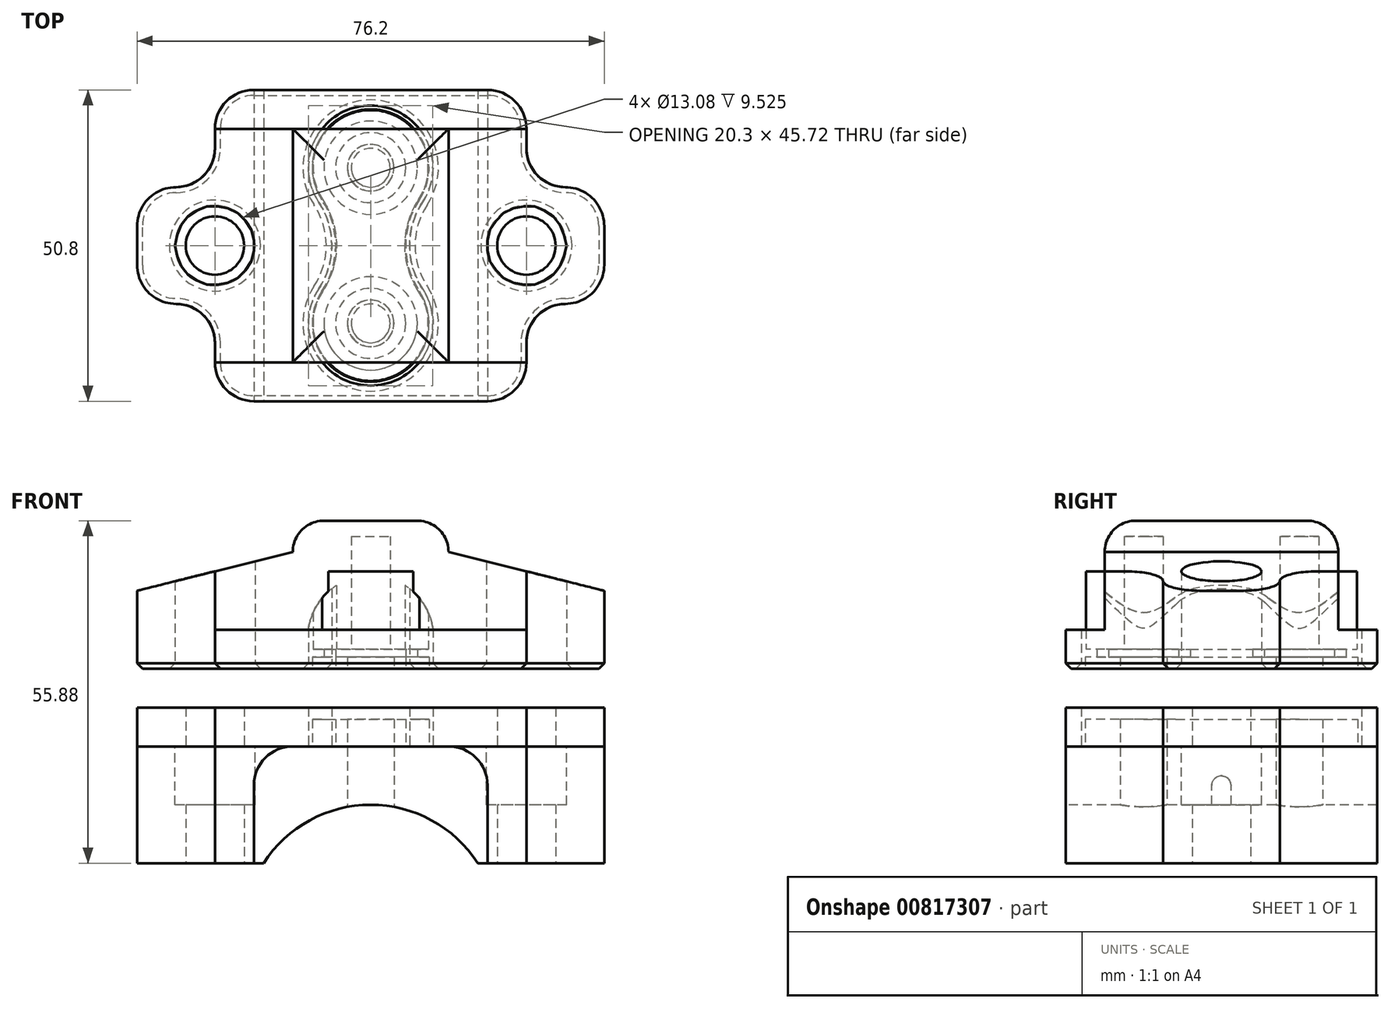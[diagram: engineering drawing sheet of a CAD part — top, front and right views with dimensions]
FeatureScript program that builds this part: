
annotation { "Feature Type Name" : "Feature", "Feature Type Description" : "" }
export const myFeature = defineFeature(function(context is Context, id is Id, definition is map)
    precondition{}
    {
        {
            var Q0;
            Q0=qCreatedBy(makeId("Top.planeOp"),FACE);
            var sketch = newSketch(context, id + "F0", { "sketchPlane" : qUnion([Q0])});
            skLineSegment(sketch, "E0.bottom", {"start": v(31.75, -9.52) * mm, "end": v(31.75, -9.52) * mm});
            skLineSegment(sketch, "E0.top", {"start": v(31.75, 9.53) * mm, "end": v(31.75, 9.53) * mm});
            skLineSegment(sketch, "E0.left", {"start": v(38.1, -3.17) * mm, "end": v(38.1, 3.17) * mm});
            skLineSegment(sketch, "E0.right", {"start": v(-38.1, -3.18) * mm, "end": v(-38.1, 3.17) * mm});
            skPoint(sketch, "E0.middle", {"position": v(0, 0) * mm});
            skLineSegment(sketch, "E1.bottom", {"start": v(19.05, -25.4) * mm, "end": v(-19.05, -25.4) * mm});
            skLineSegment(sketch, "E1.top", {"start": v(19.05, 25.4) * mm, "end": v(-19.05, 25.4) * mm});
            skLineSegment(sketch, "E1.left", {"start": v(25.4, -19.05) * mm, "end": v(25.4, -15.88) * mm});
            skLineSegment(sketch, "E1.right", {"start": v(-25.4, -19.05) * mm, "end": v(-25.4, -15.88) * mm});
            skLineSegment(sketch, "E2.trimOffspring", {"start": v(-25.4, 15.88) * mm, "end": v(-25.4, 19.05) * mm});
            skLineSegment(sketch, "E3.trimOffspring", {"start": v(-31.75, 9.52) * mm, "end": v(-31.75, 9.52) * mm});
            skLineSegment(sketch, "E4.trimOffspring", {"start": v(25.4, 15.88) * mm, "end": v(25.4, 19.05) * mm});
            skLineSegment(sketch, "E5.trimOffspring", {"start": v(-31.75, -9.53) * mm, "end": v(-31.75, -9.53) * mm});
            skCircle(sketch, "E6", {"center": v(-25.4, 0) * mm, "radius": 4.76 * mm});
            skCircle(sketch, "E7", {"center": v(25.4, 0) * mm, "radius": 4.76 * mm});
            skPoint(sketch, "E8", {"position": v(-31.75, 9.52) * mm});
            skPoint(sketch, "E9", {"position": v(31.75, 9.53) * mm});
            skPoint(sketch, "E10.visualSharp", {"position": v(-38.1, -9.53) * mm});
            skArc(sketch, "E10.filletArc", {"start": v(-38.1, -3.18) * mm, "mid": v(-36.24, -7.67) * mm, "end": v(-31.75, -9.53) * mm});
            skPoint(sketch, "E11.visualSharp", {"position": v(-38.1, 9.52) * mm});
            skArc(sketch, "E11.filletArc", {"start": v(-31.75, 9.53) * mm, "mid": v(-36.24, 7.67) * mm, "end": v(-38.1, 3.17) * mm});
            skPoint(sketch, "E12.visualSharp", {"position": v(-25.4, 9.52) * mm});
            skArc(sketch, "E12.filletArc", {"start": v(-31.75, 9.52) * mm, "mid": v(-27.26, 11.38) * mm, "end": v(-25.4, 15.88) * mm});
            skPoint(sketch, "E13.visualSharp", {"position": v(25.4, 9.53) * mm});
            skArc(sketch, "E13.filletArc", {"start": v(25.4, 15.88) * mm, "mid": v(27.26, 11.38) * mm, "end": v(31.75, 9.52) * mm});
            skPoint(sketch, "E14.visualSharp", {"position": v(38.1, 9.53) * mm});
            skArc(sketch, "E14.filletArc", {"start": v(38.1, 3.17) * mm, "mid": v(36.24, 7.67) * mm, "end": v(31.75, 9.53) * mm});
            skPoint(sketch, "E15.visualSharp", {"position": v(38.1, -9.52) * mm});
            skArc(sketch, "E15.filletArc", {"start": v(31.75, -9.53) * mm, "mid": v(36.24, -7.67) * mm, "end": v(38.1, -3.17) * mm});
            skPoint(sketch, "E16.visualSharp", {"position": v(25.4, -9.52) * mm});
            skArc(sketch, "E16.filletArc", {"start": v(31.75, -9.52) * mm, "mid": v(27.26, -11.38) * mm, "end": v(25.4, -15.88) * mm});
            skPoint(sketch, "E17.visualSharp", {"position": v(-25.4, -9.53) * mm});
            skArc(sketch, "E17.filletArc", {"start": v(-25.4, -15.88) * mm, "mid": v(-27.26, -11.38) * mm, "end": v(-31.75, -9.53) * mm});
            skPoint(sketch, "E18.visualSharp", {"position": v(25.4, 25.4) * mm});
            skArc(sketch, "E18.filletArc", {"start": v(25.4, 19.05) * mm, "mid": v(23.54, 23.54) * mm, "end": v(19.05, 25.4) * mm});
            skPoint(sketch, "E19.visualSharp", {"position": v(25.4, -25.4) * mm});
            skArc(sketch, "E19.filletArc", {"start": v(19.05, -25.4) * mm, "mid": v(23.54, -23.54) * mm, "end": v(25.4, -19.05) * mm});
            skPoint(sketch, "E20.visualSharp", {"position": v(-25.4, -25.4) * mm});
            skArc(sketch, "E20.filletArc", {"start": v(-25.4, -19.05) * mm, "mid": v(-23.54, -23.54) * mm, "end": v(-19.05, -25.4) * mm});
            skPoint(sketch, "E21.visualSharp", {"position": v(-25.4, 25.4) * mm});
            skArc(sketch, "E21.filletArc", {"start": v(-19.05, 25.4) * mm, "mid": v(-23.54, 23.54) * mm, "end": v(-25.4, 19.05) * mm});
            skCircle(sketch, "E22", {"center": v(0, 12.7) * mm, "radius": 3.18 * mm, "construction": true});
            skCircle(sketch, "E23", {"center": v(0, -12.7) * mm, "radius": 3.18 * mm, "construction": true});
            skArc(sketch, "E24", {"start": v(8.48, 7.1) * mm, "mid": v(0, 22.86) * mm, "end": v(-8.48, 7.1) * mm});
            skArc(sketch, "E25", {"start": v(-8.48, -7.1) * mm, "mid": v(0, -22.86) * mm, "end": v(8.48, -7.1) * mm});
            skArc(sketch, "E26", {"start": v(8.48, 7.1) * mm, "mid": v(6.35, 0) * mm, "end": v(8.48, -7.1) * mm});
            skArc(sketch, "E27", {"start": v(-8.48, -7.1) * mm, "mid": v(-6.35, 0) * mm, "end": v(-8.48, 7.1) * mm});
            skSolve(sketch);
        }
        {
            var Q0;
            Q0 = qSketchRegion(id + "F0", true);
            extrude(context, id + "F1", {"entities" : qUnion([Q0]), "depth" : 25.4 * mm, "offsetDistance" : 25.4 * mm});
        }
        {
            var Q0;
            Q0=qCreatedBy(makeId("Front.planeOp"),FACE);
            var sketch = newSketch(context, id + "F2", { "sketchPlane" : qUnion([Q0])});
            skLineSegment(sketch, "E28.bottom", {"start": v(19.05, -19.05) * mm, "end": v(-19.05, -19.05) * mm});
            skLineSegment(sketch, "E28.top", {"start": v(12.7, 19.05) * mm, "end": v(-12.7, 19.05) * mm});
            skLineSegment(sketch, "E28.left", {"start": v(19.05, -19.05) * mm, "end": v(19.05, 12.7) * mm});
            skLineSegment(sketch, "E28.right", {"start": v(-19.05, -19.05) * mm, "end": v(-19.05, 12.7) * mm});
            skPoint(sketch, "E28.middle", {"position": v(0, 0) * mm});
            skPoint(sketch, "E29.visualSharp", {"position": v(-19.05, 19.05) * mm});
            skArc(sketch, "E29.filletArc", {"start": v(-12.7, 19.05) * mm, "mid": v(-17.2, 17.2) * mm, "end": v(-19.05, 12.7) * mm});
            skPoint(sketch, "E30.visualSharp", {"position": v(19.05, 19.05) * mm});
            skArc(sketch, "E30.filletArc", {"start": v(19.05, 12.7) * mm, "mid": v(17.2, 17.2) * mm, "end": v(12.7, 19.05) * mm});
            skSolve(sketch);
        }
        {
            var Q0;
            Q0 = qSketchRegion(id + "F2", true);
            extrude(context, id + "F3", {"entities" : qUnion([Q0]), "operationType" : NewBodyOperationType.REMOVE, "endBound" : BoundingType.SYMMETRIC, "oppositeDirection" : true, "depth" : 127 * mm, "offsetDistance" : 25.4 * mm});
        }
        {
            var Q0;
            Q0=makeQuery(id+"F1.opExtrude","CAP_FACE",FACE,{"disambiguationData":[OSD([sQuery(id+"F0.wireOp",EDGE,"E0.left"),sQuery(id+"F0.wireOp",EDGE,"E0.right"),sQuery(id+"F0.wireOp",EDGE,"E1.bottom"),sQuery(id+"F0.wireOp",EDGE,"E1.top"),sQuery(id+"F0.wireOp",EDGE,"E1.left"),sQuery(id+"F0.wireOp",EDGE,"E1.right"),sQuery(id+"F0.wireOp",EDGE,"E2.trimOffspring"),sQuery(id+"F0.wireOp",EDGE,"E4.trimOffspring"),sQuery(id+"F0.wireOp",EDGE,"E6"),sQuery(id+"F0.wireOp",EDGE,"E7"),sQuery(id+"F0.wireOp",EDGE,"E10.filletArc"),sQuery(id+"F0.wireOp",EDGE,"E11.filletArc"),sQuery(id+"F0.wireOp",EDGE,"E12.filletArc"),sQuery(id+"F0.wireOp",EDGE,"E13.filletArc"),sQuery(id+"F0.wireOp",EDGE,"E14.filletArc"),sQuery(id+"F0.wireOp",EDGE,"E15.filletArc"),sQuery(id+"F0.wireOp",EDGE,"E16.filletArc"),sQuery(id+"F0.wireOp",EDGE,"E17.filletArc"),sQuery(id+"F0.wireOp",EDGE,"E18.filletArc"),sQuery(id+"F0.wireOp",EDGE,"E19.filletArc"),sQuery(id+"F0.wireOp",EDGE,"E20.filletArc"),sQuery(id+"F0.wireOp",EDGE,"E21.filletArc"),sQuery(id+"F0.wireOp",EDGE,"E24"),sQuery(id+"F0.wireOp",EDGE,"E25"),sQuery(id+"F0.wireOp",EDGE,"E26"),sQuery(id+"F0.wireOp",EDGE,"E27")])],"isStart":false});
            cPlane(context, id + "F4", {"entities" : qUnion([Q0]), "cplaneType" : CPlaneType.OFFSET, "offset" : 6.35 * mm, "width" : 152.4 * mm, "height" : 152.4 * mm});
        }
        {
            var Q0;
            Q0=qCreatedBy(id+"F4.planeOp",FACE);
            var sketch = newSketch(context, id + "F5", { "sketchPlane" : qUnion([Q0])});
            skArc(sketch, "E31.0.0", {"start": v(-25.4, 15.88) * mm, "mid": v(-27.26, 11.38) * mm, "end": v(-31.75, 9.52) * mm});
            skArc(sketch, "E31.0.1", {"start": v(-31.75, 9.53) * mm, "mid": v(-36.24, 7.67) * mm, "end": v(-38.1, 3.17) * mm});
            skLineSegment(sketch, "E31.0.2", {"start": v(-38.1, 3.17) * mm, "end": v(-38.1, -3.18) * mm});
            skArc(sketch, "E31.0.3", {"start": v(-38.1, -3.18) * mm, "mid": v(-36.24, -7.67) * mm, "end": v(-31.75, -9.53) * mm});
            skArc(sketch, "E31.0.4", {"start": v(-31.75, -9.53) * mm, "mid": v(-27.26, -11.38) * mm, "end": v(-25.4, -15.88) * mm});
            skLineSegment(sketch, "E31.0.5", {"start": v(-25.4, -15.88) * mm, "end": v(-25.4, -19.05) * mm});
            skArc(sketch, "E31.0.6", {"start": v(-25.4, -19.05) * mm, "mid": v(-23.54, -23.54) * mm, "end": v(-19.05, -25.4) * mm});
            skLineSegment(sketch, "E31.0.7", {"start": v(-19.05, -25.4) * mm, "end": v(19.05, -25.4) * mm});
            skArc(sketch, "E31.0.8", {"start": v(19.05, -25.4) * mm, "mid": v(23.54, -23.54) * mm, "end": v(25.4, -19.05) * mm});
            skLineSegment(sketch, "E31.0.9", {"start": v(25.4, -19.05) * mm, "end": v(25.4, -15.88) * mm});
            skArc(sketch, "E31.0.10", {"start": v(25.4, -15.88) * mm, "mid": v(27.26, -11.38) * mm, "end": v(31.75, -9.52) * mm});
            skArc(sketch, "E31.0.11", {"start": v(31.75, -9.53) * mm, "mid": v(36.24, -7.67) * mm, "end": v(38.1, -3.17) * mm});
            skLineSegment(sketch, "E31.0.12", {"start": v(38.1, -3.17) * mm, "end": v(38.1, 3.17) * mm});
            skArc(sketch, "E31.0.13", {"start": v(38.1, 3.17) * mm, "mid": v(36.24, 7.67) * mm, "end": v(31.75, 9.53) * mm});
            skArc(sketch, "E31.0.14", {"start": v(31.75, 9.52) * mm, "mid": v(27.26, 11.38) * mm, "end": v(25.4, 15.88) * mm});
            skLineSegment(sketch, "E31.0.15", {"start": v(25.4, 15.88) * mm, "end": v(25.4, 19.05) * mm});
            skArc(sketch, "E31.0.16", {"start": v(25.4, 19.05) * mm, "mid": v(23.54, 23.54) * mm, "end": v(19.05, 25.4) * mm});
            skLineSegment(sketch, "E31.0.17", {"start": v(19.05, 25.4) * mm, "end": v(-19.05, 25.4) * mm});
            skArc(sketch, "E31.0.18", {"start": v(-19.05, 25.4) * mm, "mid": v(-23.54, 23.54) * mm, "end": v(-25.4, 19.05) * mm});
            skLineSegment(sketch, "E31.0.19", {"start": v(-25.4, 19.05) * mm, "end": v(-25.4, 15.88) * mm});
            skCircle(sketch, "E32.0", {"center": v(25.4, 0) * mm, "radius": 4.76 * mm, "construction": true});
            skCircle(sketch, "E33.0", {"center": v(-25.4, 0) * mm, "radius": 4.76 * mm, "construction": true});
            skArc(sketch, "E34.0", {"start": v(8.48, 7.1) * mm, "mid": v(0, 22.86) * mm, "end": v(-8.48, 7.1) * mm});
            skArc(sketch, "E35.0", {"start": v(8.48, 7.1) * mm, "mid": v(6.35, 0) * mm, "end": v(8.48, -7.1) * mm});
            skArc(sketch, "E36.0", {"start": v(-8.48, -7.1) * mm, "mid": v(-6.35, 0) * mm, "end": v(-8.48, 7.1) * mm});
            skArc(sketch, "E37.0", {"start": v(-8.48, -7.1) * mm, "mid": v(0, -22.86) * mm, "end": v(8.48, -7.1) * mm});
            skCircle(sketch, "E38", {"center": v(25.4, 0) * mm, "radius": 6.54 * mm});
            skCircle(sketch, "E39", {"center": v(-25.4, 0) * mm, "radius": 6.54 * mm});
            skSolve(sketch);
        }
        {
            var Q0;
            Q0 = qSketchRegion(id + "F5", true);
            extrude(context, id + "F6", {"entities" : qUnion([Q0]), "depth" : 6.35 * mm, "offsetDistance" : 25.4 * mm});
        }
        {
            var Q0;
            Q0=qCreatedBy(id+"F4.planeOp",FACE);
            cPlane(context, id + "F7", {"entities" : qUnion([Q0]), "cplaneType" : CPlaneType.OFFSET, "offset" : 3.17 * mm, "width" : 152.4 * mm, "height" : 152.4 * mm});
        }
        {
            var Q0;
            Q0=qCreatedBy(id+"F7.planeOp",FACE);
            var sketch = newSketch(context, id + "F8", { "sketchPlane" : qUnion([Q0])});
            skArc(sketch, "E40.0", {"start": v(-8.48, -7.1) * mm, "mid": v(0, -22.86) * mm, "end": v(8.48, -7.1) * mm, "construction": true});
            skArc(sketch, "E41.0", {"start": v(8.48, 7.1) * mm, "mid": v(6.35, 0) * mm, "end": v(8.48, -7.1) * mm, "construction": true});
            skArc(sketch, "E42.0", {"start": v(-8.48, -7.1) * mm, "mid": v(-6.35, 0) * mm, "end": v(-8.48, 7.1) * mm, "construction": true});
            skArc(sketch, "E43.0", {"start": v(8.48, 7.1) * mm, "mid": v(0, 22.86) * mm, "end": v(-8.48, 7.1) * mm, "construction": true});
            skArc(sketch, "E44.0", {"start": v(-7.85, -7.53) * mm, "mid": v(0, -22.1) * mm, "end": v(7.85, -7.53) * mm});
            skArc(sketch, "E44.1", {"start": v(-7.85, -7.53) * mm, "mid": v(-5.59, 0) * mm, "end": v(-7.85, 7.53) * mm});
            skArc(sketch, "E44.2", {"start": v(7.85, 7.53) * mm, "mid": v(0, 22.1) * mm, "end": v(-7.85, 7.53) * mm});
            skArc(sketch, "E44.3", {"start": v(7.85, 7.53) * mm, "mid": v(5.59, 0) * mm, "end": v(7.85, -7.53) * mm});
            skSolve(sketch);
        }
        {
            var Q0;
            Q0 = qSketchRegion(id + "F8", true);
            extrude(context, id + "F9", {"entities" : qUnion([Q0]), "depth" : 12.7 * mm, "offsetDistance" : 25.4 * mm});
        }
        {
            var Q0;
            Q0=qCreatedBy(makeId("Top.planeOp"),FACE);
            var sketch = newSketch(context, id + "F10", { "sketchPlane" : qUnion([Q0])});
            skArc(sketch, "E45.0.0", {"start": v(-19.05, 25.4) * mm, "mid": v(-23.54, 23.54) * mm, "end": v(-25.4, 19.05) * mm});
            skLineSegment(sketch, "E45.0.1", {"start": v(-25.4, 19.05) * mm, "end": v(-25.4, 15.88) * mm});
            skArc(sketch, "E45.0.2", {"start": v(-25.4, 15.88) * mm, "mid": v(-27.26, 11.38) * mm, "end": v(-31.75, 9.52) * mm});
            skArc(sketch, "E45.0.3", {"start": v(-31.75, 9.53) * mm, "mid": v(-36.24, 7.67) * mm, "end": v(-38.1, 3.17) * mm});
            skLineSegment(sketch, "E45.0.4", {"start": v(-38.1, 3.17) * mm, "end": v(-38.1, -3.18) * mm});
            skArc(sketch, "E45.0.5", {"start": v(-38.1, -3.18) * mm, "mid": v(-36.24, -7.67) * mm, "end": v(-31.75, -9.53) * mm});
            skArc(sketch, "E45.0.6", {"start": v(-31.75, -9.52) * mm, "mid": v(-27.26, -11.38) * mm, "end": v(-25.4, -15.88) * mm});
            skLineSegment(sketch, "E45.0.7", {"start": v(-25.4, -15.88) * mm, "end": v(-25.4, -19.05) * mm});
            skArc(sketch, "E45.0.8", {"start": v(-25.4, -19.05) * mm, "mid": v(-23.54, -23.54) * mm, "end": v(-19.05, -25.4) * mm});
            skLineSegment(sketch, "E45.0.9", {"start": v(-19.05, -25.4) * mm, "end": v(19.05, -25.4) * mm});
            skArc(sketch, "E45.0.10", {"start": v(19.05, -25.4) * mm, "mid": v(23.54, -23.54) * mm, "end": v(25.4, -19.05) * mm});
            skLineSegment(sketch, "E45.0.11", {"start": v(25.4, -19.05) * mm, "end": v(25.4, -15.88) * mm});
            skArc(sketch, "E45.0.12", {"start": v(25.4, -15.88) * mm, "mid": v(27.26, -11.38) * mm, "end": v(31.75, -9.52) * mm});
            skArc(sketch, "E45.0.13", {"start": v(31.75, -9.53) * mm, "mid": v(36.24, -7.67) * mm, "end": v(38.1, -3.17) * mm});
            skLineSegment(sketch, "E45.0.14", {"start": v(38.1, -3.17) * mm, "end": v(38.1, 3.17) * mm});
            skArc(sketch, "E45.0.15", {"start": v(38.1, 3.17) * mm, "mid": v(36.24, 7.67) * mm, "end": v(31.75, 9.53) * mm});
            skArc(sketch, "E45.0.16", {"start": v(31.75, 9.52) * mm, "mid": v(27.26, 11.38) * mm, "end": v(25.4, 15.88) * mm});
            skLineSegment(sketch, "E45.0.17", {"start": v(25.4, 15.88) * mm, "end": v(25.4, 19.05) * mm});
            skArc(sketch, "E45.0.18", {"start": v(25.4, 19.05) * mm, "mid": v(23.54, 23.54) * mm, "end": v(19.05, 25.4) * mm});
            skLineSegment(sketch, "E45.0.19", {"start": v(19.05, 25.4) * mm, "end": v(-19.05, 25.4) * mm});
            skCircle(sketch, "E46.0", {"center": v(25.4, 0) * mm, "radius": 4.76 * mm});
            skCircle(sketch, "E47.0", {"center": v(-25.4, 0) * mm, "radius": 4.76 * mm});
            skCircle(sketch, "E48", {"center": v(0, 12.7) * mm, "radius": 3.81 * mm});
            skCircle(sketch, "E49", {"center": v(0, -12.7) * mm, "radius": 3.81 * mm});
            skSolve(sketch);
        }
        {
            var Q0;
            Q0 = qSketchRegion(id + "F10", true);
            extrude(context, id + "F11", {"entities" : qUnion([Q0]), "depth" : 19.05 * mm, "offsetDistance" : 25.4 * mm});
        }
        {
            var Q0;
            Q0=makeQuery(id+"F11.opExtrude","CAP_FACE",FACE,{"disambiguationData":[OSD([sQuery(id+"F10.wireOp",EDGE,"E45.0.0"),sQuery(id+"F10.wireOp",EDGE,"E45.0.1"),sQuery(id+"F10.wireOp",EDGE,"E45.0.2"),sQuery(id+"F10.wireOp",EDGE,"E45.0.3"),sQuery(id+"F10.wireOp",EDGE,"E45.0.4"),sQuery(id+"F10.wireOp",EDGE,"E45.0.5"),sQuery(id+"F10.wireOp",EDGE,"E45.0.6"),sQuery(id+"F10.wireOp",EDGE,"E45.0.7"),sQuery(id+"F10.wireOp",EDGE,"E45.0.8"),sQuery(id+"F10.wireOp",EDGE,"E45.0.9"),sQuery(id+"F10.wireOp",EDGE,"E45.0.10"),sQuery(id+"F10.wireOp",EDGE,"E45.0.11"),sQuery(id+"F10.wireOp",EDGE,"E45.0.12"),sQuery(id+"F10.wireOp",EDGE,"E45.0.13"),sQuery(id+"F10.wireOp",EDGE,"E45.0.14"),sQuery(id+"F10.wireOp",EDGE,"E45.0.15"),sQuery(id+"F10.wireOp",EDGE,"E45.0.16"),sQuery(id+"F10.wireOp",EDGE,"E45.0.17"),sQuery(id+"F10.wireOp",EDGE,"E45.0.18"),sQuery(id+"F10.wireOp",EDGE,"E45.0.19"),sQuery(id+"F10.wireOp",EDGE,"E46.0"),sQuery(id+"F10.wireOp",EDGE,"E47.0")])],"isStart":false});
            var sketch = newSketch(context, id + "F12", { "sketchPlane" : qUnion([Q0])});
            skArc(sketch, "E50.0", {"start": v(-8.48, -7.1) * mm, "mid": v(0, -22.86) * mm, "end": v(8.48, -7.1) * mm, "construction": true});
            skArc(sketch, "E51.0", {"start": v(8.48, 7.1) * mm, "mid": v(6.35, 0) * mm, "end": v(8.48, -7.1) * mm, "construction": true});
            skArc(sketch, "E52.0", {"start": v(8.48, 7.1) * mm, "mid": v(0, 22.86) * mm, "end": v(-8.48, 7.1) * mm, "construction": true});
            skArc(sketch, "E53.0", {"start": v(-8.48, -7.1) * mm, "mid": v(-6.35, 0) * mm, "end": v(-8.48, 7.1) * mm, "construction": true});
            skCircle(sketch, "E54.0", {"center": v(0, -12.7) * mm, "radius": 3.81 * mm});
            skCircle(sketch, "E55.0", {"center": v(0, 12.7) * mm, "radius": 3.81 * mm});
            skArc(sketch, "E56.0", {"start": v(-7.95, -7.46) * mm, "mid": v(0, -22.23) * mm, "end": v(7.95, -7.46) * mm});
            skArc(sketch, "E56.1", {"start": v(-7.95, -7.46) * mm, "mid": v(-5.72, 0) * mm, "end": v(-7.95, 7.46) * mm});
            skArc(sketch, "E56.2", {"start": v(7.95, 7.46) * mm, "mid": v(0, 22.23) * mm, "end": v(-7.95, 7.46) * mm});
            skArc(sketch, "E56.3", {"start": v(7.95, 7.46) * mm, "mid": v(5.72, 0) * mm, "end": v(7.95, -7.46) * mm});
            skSolve(sketch);
        }
        {
            var Q0;
            Q0 = qSketchRegion(id + "F12", true);
            extrude(context, id + "F13", {"entities" : qUnion([Q0]), "operationType" : NewBodyOperationType.ADD, "depth" : 4.44 * mm, "offsetDistance" : 25.4 * mm});
        }
        {
            var Q0;
            Q0=qCreatedBy(makeId("Front.planeOp"),FACE);
            var sketch = newSketch(context, id + "F14", { "sketchPlane" : qUnion([Q0])});
            skArc(sketch, "E57", {"start": v(17.46, 0) * mm, "mid": v(0, 9.53) * mm, "end": v(-17.46, 0) * mm});
            skLineSegment(sketch, "E58", {"start": v(-17.46, 0) * mm, "end": v(17.46, 0) * mm});
            skSolve(sketch);
        }
        {
            var Q0;
            Q0 = qSketchRegion(id + "F14", true);
            extrude(context, id + "F15", {"entities" : qUnion([Q0]), "operationType" : NewBodyOperationType.REMOVE, "endBound" : BoundingType.SYMMETRIC, "oppositeDirection" : true, "depth" : 127 * mm, "offsetDistance" : 25.4 * mm});
        }
        {
            var Q0;
            Q0=makeQuery(id+"F6.opExtrude","CAP_FACE",FACE,{"disambiguationData":[OSD([sQuery(id+"F5.wireOp",EDGE,"E31.0.0"),sQuery(id+"F5.wireOp",EDGE,"E31.0.1"),sQuery(id+"F5.wireOp",EDGE,"E31.0.2"),sQuery(id+"F5.wireOp",EDGE,"E31.0.3"),sQuery(id+"F5.wireOp",EDGE,"E31.0.4"),sQuery(id+"F5.wireOp",EDGE,"E31.0.5"),sQuery(id+"F5.wireOp",EDGE,"E31.0.6"),sQuery(id+"F5.wireOp",EDGE,"E31.0.7"),sQuery(id+"F5.wireOp",EDGE,"E31.0.8"),sQuery(id+"F5.wireOp",EDGE,"E31.0.9"),sQuery(id+"F5.wireOp",EDGE,"E31.0.10"),sQuery(id+"F5.wireOp",EDGE,"E31.0.11"),sQuery(id+"F5.wireOp",EDGE,"E31.0.12"),sQuery(id+"F5.wireOp",EDGE,"E31.0.13"),sQuery(id+"F5.wireOp",EDGE,"E31.0.14"),sQuery(id+"F5.wireOp",EDGE,"E31.0.15"),sQuery(id+"F5.wireOp",EDGE,"E31.0.16"),sQuery(id+"F5.wireOp",EDGE,"E31.0.17"),sQuery(id+"F5.wireOp",EDGE,"E31.0.18"),sQuery(id+"F5.wireOp",EDGE,"E31.0.19"),sQuery(id+"F5.wireOp",EDGE,"E34.0"),sQuery(id+"F5.wireOp",EDGE,"E35.0"),sQuery(id+"F5.wireOp",EDGE,"E36.0"),sQuery(id+"F5.wireOp",EDGE,"E37.0"),sQuery(id+"F5.wireOp",EDGE,"E38"),sQuery(id+"F5.wireOp",EDGE,"E39")])],"isStart":true});
            var sketch = newSketch(context, id + "F16", { "sketchPlane" : qUnion([Q0])});
            skArc(sketch, "E59.0", {"start": v(7.95, -7.46) * mm, "mid": v(5.72, 0) * mm, "end": v(7.95, 7.46) * mm});
            skArc(sketch, "E60.0", {"start": v(7.95, -7.46) * mm, "mid": v(0, -22.23) * mm, "end": v(-7.95, -7.46) * mm});
            skArc(sketch, "E61.0", {"start": v(-7.95, 7.46) * mm, "mid": v(-5.72, 0) * mm, "end": v(-7.95, -7.46) * mm});
            skArc(sketch, "E62.0", {"start": v(-7.95, 7.46) * mm, "mid": v(0, 22.23) * mm, "end": v(7.95, 7.46) * mm});
            skCircle(sketch, "E63.0", {"center": v(0, 12.7) * mm, "radius": 3.81 * mm});
            skCircle(sketch, "E64.0", {"center": v(0, -12.7) * mm, "radius": 3.81 * mm});
            skSolve(sketch);
        }
        {
            var Q0;
            Q0 = qSketchRegion(id + "F16", true);
            extrude(context, id + "F17", {"entities" : qUnion([Q0]), "oppositeDirection" : true, "depth" : 1.9 * mm, "offsetDistance" : 25.4 * mm});
        }
        {
            var Q0;
            Q0=makeQuery(id+"F6.opExtrude","CAP_FACE",FACE,{"disambiguationData":[OSD([sQuery(id+"F5.wireOp",EDGE,"E31.0.0"),sQuery(id+"F5.wireOp",EDGE,"E31.0.1"),sQuery(id+"F5.wireOp",EDGE,"E31.0.2"),sQuery(id+"F5.wireOp",EDGE,"E31.0.3"),sQuery(id+"F5.wireOp",EDGE,"E31.0.4"),sQuery(id+"F5.wireOp",EDGE,"E31.0.5"),sQuery(id+"F5.wireOp",EDGE,"E31.0.6"),sQuery(id+"F5.wireOp",EDGE,"E31.0.7"),sQuery(id+"F5.wireOp",EDGE,"E31.0.8"),sQuery(id+"F5.wireOp",EDGE,"E31.0.9"),sQuery(id+"F5.wireOp",EDGE,"E31.0.10"),sQuery(id+"F5.wireOp",EDGE,"E31.0.11"),sQuery(id+"F5.wireOp",EDGE,"E31.0.12"),sQuery(id+"F5.wireOp",EDGE,"E31.0.13"),sQuery(id+"F5.wireOp",EDGE,"E31.0.14"),sQuery(id+"F5.wireOp",EDGE,"E31.0.15"),sQuery(id+"F5.wireOp",EDGE,"E31.0.16"),sQuery(id+"F5.wireOp",EDGE,"E31.0.17"),sQuery(id+"F5.wireOp",EDGE,"E31.0.18"),sQuery(id+"F5.wireOp",EDGE,"E31.0.19"),sQuery(id+"F5.wireOp",EDGE,"E34.0"),sQuery(id+"F5.wireOp",EDGE,"E35.0"),sQuery(id+"F5.wireOp",EDGE,"E36.0"),sQuery(id+"F5.wireOp",EDGE,"E37.0"),sQuery(id+"F5.wireOp",EDGE,"E38"),sQuery(id+"F5.wireOp",EDGE,"E39")])],"isStart":true});
            var sketch = newSketch(context, id + "F18", { "sketchPlane" : qUnion([Q0])});
            skCircle(sketch, "E65", {"center": v(0, 12.7) * mm, "radius": 3.18 * mm});
            skCircle(sketch, "E66", {"center": v(0, -12.7) * mm, "radius": 3.18 * mm});
            skSolve(sketch);
        }
        {
            var Q0;
            Q0 = qSketchRegion(id + "F18", true);
            extrude(context, id + "F19", {"entities" : qUnion([Q0]), "oppositeDirection" : true, "depth" : 15.24 * mm, "offsetDistance" : 25.4 * mm});
        }
        {
            var Q0;
            Q0=makeQuery(id+"F19.opExtrude","CAP_FACE",FACE,{"disambiguationData":[OSD([sQuery(id+"F18.wireOp",EDGE,"E65")])],"isStart":false});
            var sketch = newSketch(context, id + "F20", { "sketchPlane" : qUnion([Q0])});
            skCircle(sketch, "E67", {"center": v(0, -12.7) * mm, "radius": 4.76 * mm});
            skCircle(sketch, "E68", {"center": v(0, 12.7) * mm, "radius": 4.76 * mm});
            skSolve(sketch);
        }
        {
            var Q0;
            Q0 = qSketchRegion(id + "F20", true);
            extrude(context, id + "F21", {"entities" : qUnion([Q0]), "operationType" : NewBodyOperationType.ADD, "depth" : 3.8 * mm, "offsetDistance" : 25.4 * mm});
        }
        {
            var Q0;
            Q0=makeQuery(id+"F11.opExtrude","CAP_FACE",FACE,{"disambiguationData":[OSD([sQuery(id+"F10.wireOp",EDGE,"E45.0.0"),sQuery(id+"F10.wireOp",EDGE,"E45.0.1"),sQuery(id+"F10.wireOp",EDGE,"E45.0.2"),sQuery(id+"F10.wireOp",EDGE,"E45.0.3"),sQuery(id+"F10.wireOp",EDGE,"E45.0.4"),sQuery(id+"F10.wireOp",EDGE,"E45.0.5"),sQuery(id+"F10.wireOp",EDGE,"E45.0.6"),sQuery(id+"F10.wireOp",EDGE,"E45.0.7"),sQuery(id+"F10.wireOp",EDGE,"E45.0.8"),sQuery(id+"F10.wireOp",EDGE,"E45.0.9"),sQuery(id+"F10.wireOp",EDGE,"E45.0.10"),sQuery(id+"F10.wireOp",EDGE,"E45.0.11"),sQuery(id+"F10.wireOp",EDGE,"E45.0.12"),sQuery(id+"F10.wireOp",EDGE,"E45.0.13"),sQuery(id+"F10.wireOp",EDGE,"E45.0.14"),sQuery(id+"F10.wireOp",EDGE,"E45.0.15"),sQuery(id+"F10.wireOp",EDGE,"E45.0.16"),sQuery(id+"F10.wireOp",EDGE,"E45.0.17"),sQuery(id+"F10.wireOp",EDGE,"E45.0.18"),sQuery(id+"F10.wireOp",EDGE,"E45.0.19"),sQuery(id+"F10.wireOp",EDGE,"E46.0"),sQuery(id+"F10.wireOp",EDGE,"E47.0"),sQuery(id+"F10.wireOp",EDGE,"E48"),sQuery(id+"F10.wireOp",EDGE,"E49")])],"isStart":false});
            var sketch = newSketch(context, id + "F22", { "sketchPlane" : qUnion([Q0])});
            skCircle(sketch, "E69.0", {"center": v(25.4, 0) * mm, "radius": 6.54 * mm});
            skCircle(sketch, "E70.0", {"center": v(-25.4, 0) * mm, "radius": 6.54 * mm});
            skSolve(sketch);
        }
        {
            var Q0;
            Q0 = qSketchRegion(id + "F22", true);
            extrude(context, id + "F23", {"entities" : qUnion([Q0]), "operationType" : NewBodyOperationType.REMOVE, "oppositeDirection" : true, "depth" : 9.52 * mm, "offsetDistance" : 25.4 * mm});
        }
        {
            var Q0;
            Q0=makeQuery(id+"F6.opExtrude","CAP_FACE",FACE,{"disambiguationData":[OSD([sQuery(id+"F5.wireOp",EDGE,"E31.0.0"),sQuery(id+"F5.wireOp",EDGE,"E31.0.1"),sQuery(id+"F5.wireOp",EDGE,"E31.0.2"),sQuery(id+"F5.wireOp",EDGE,"E31.0.3"),sQuery(id+"F5.wireOp",EDGE,"E31.0.4"),sQuery(id+"F5.wireOp",EDGE,"E31.0.5"),sQuery(id+"F5.wireOp",EDGE,"E31.0.6"),sQuery(id+"F5.wireOp",EDGE,"E31.0.7"),sQuery(id+"F5.wireOp",EDGE,"E31.0.8"),sQuery(id+"F5.wireOp",EDGE,"E31.0.9"),sQuery(id+"F5.wireOp",EDGE,"E31.0.10"),sQuery(id+"F5.wireOp",EDGE,"E31.0.11"),sQuery(id+"F5.wireOp",EDGE,"E31.0.12"),sQuery(id+"F5.wireOp",EDGE,"E31.0.13"),sQuery(id+"F5.wireOp",EDGE,"E31.0.14"),sQuery(id+"F5.wireOp",EDGE,"E31.0.15"),sQuery(id+"F5.wireOp",EDGE,"E31.0.16"),sQuery(id+"F5.wireOp",EDGE,"E31.0.17"),sQuery(id+"F5.wireOp",EDGE,"E31.0.18"),sQuery(id+"F5.wireOp",EDGE,"E31.0.19"),sQuery(id+"F5.wireOp",EDGE,"E34.0"),sQuery(id+"F5.wireOp",EDGE,"E35.0"),sQuery(id+"F5.wireOp",EDGE,"E36.0"),sQuery(id+"F5.wireOp",EDGE,"E37.0"),sQuery(id+"F5.wireOp",EDGE,"E38"),sQuery(id+"F5.wireOp",EDGE,"E39")])],"isStart":false});
            var sketch = newSketch(context, id + "F24", { "sketchPlane" : qUnion([Q0])});
            skCircle(sketch, "E71.0", {"center": v(-25.4, 0) * mm, "radius": 6.54 * mm});
            skCircle(sketch, "E72.0", {"center": v(25.4, 0) * mm, "radius": 6.54 * mm});
            skArc(sketch, "E73.0", {"start": v(-31.75, 9.53) * mm, "mid": v(-36.24, 7.67) * mm, "end": v(-38.1, 3.17) * mm});
            skArc(sketch, "E74.0", {"start": v(-38.1, -3.18) * mm, "mid": v(-36.24, -7.67) * mm, "end": v(-31.75, -9.53) * mm});
            skArc(sketch, "E75.0", {"start": v(-31.75, -9.52) * mm, "mid": v(-27.26, -11.38) * mm, "end": v(-25.4, -15.88) * mm});
            skArc(sketch, "E76.0", {"start": v(-25.4, 15.88) * mm, "mid": v(-27.26, 11.38) * mm, "end": v(-31.75, 9.52) * mm});
            skArc(sketch, "E77.0", {"start": v(25.4, -15.88) * mm, "mid": v(27.26, -11.38) * mm, "end": v(31.75, -9.52) * mm});
            skArc(sketch, "E78.0", {"start": v(31.75, -9.53) * mm, "mid": v(36.24, -7.67) * mm, "end": v(38.1, -3.17) * mm});
            skPoint(sketch, "E79.0", {"position": v(38.1, 3.17) * mm});
            skPoint(sketch, "E80.0", {"position": v(31.75, 9.53) * mm});
            skArc(sketch, "E81.0", {"start": v(31.75, 9.52) * mm, "mid": v(27.26, 11.38) * mm, "end": v(25.4, 15.88) * mm});
            skArc(sketch, "E82.0", {"start": v(38.1, 3.17) * mm, "mid": v(36.24, 7.67) * mm, "end": v(31.75, 9.53) * mm});
            skLineSegment(sketch, "E83.0", {"start": v(38.1, -3.17) * mm, "end": v(38.1, 3.17) * mm});
            skLineSegment(sketch, "E84.0", {"start": v(-25.4, -15.88) * mm, "end": v(-25.4, -19.05) * mm});
            skLineSegment(sketch, "E85.0.0", {"start": v(-25.4, 19.05) * mm, "end": v(-25.4, 15.88) * mm});
            skLineSegment(sketch, "E85.0.2", {"start": v(-25.4, 15.88) * mm, "end": v(-25.4, 19.05) * mm});
            skLineSegment(sketch, "E86.0", {"start": v(25.4, 15.88) * mm, "end": v(25.4, 19.05) * mm});
            skLineSegment(sketch, "E87.0", {"start": v(25.4, -19.05) * mm, "end": v(25.4, -15.88) * mm});
            skLineSegment(sketch, "E88", {"start": v(-25.4, -19.05) * mm, "end": v(-7.93, -19.05) * mm});
            skLineSegment(sketch, "E89", {"start": v(-25.4, 19.05) * mm, "end": v(-7.93, 19.05) * mm});
            skArc(sketch, "E90.0", {"start": v(8.48, 7.1) * mm, "mid": v(10.15, 13.17) * mm, "end": v(7.93, 19.05) * mm});
            skArc(sketch, "E91.0", {"start": v(-8.48, -7.1) * mm, "mid": v(-6.35, 0) * mm, "end": v(-8.48, 7.1) * mm});
            skArc(sketch, "E92.0", {"start": v(-8.48, -7.1) * mm, "mid": v(-10.15, -13.17) * mm, "end": v(-7.93, -19.05) * mm});
            skArc(sketch, "E93.0", {"start": v(8.48, 7.1) * mm, "mid": v(6.35, 0) * mm, "end": v(8.48, -7.1) * mm});
            skArc(sketch, "E94.trimOffspring", {"start": v(7.93, -19.05) * mm, "mid": v(10.15, -13.17) * mm, "end": v(8.48, -7.1) * mm});
            skArc(sketch, "E95.trimOffspring", {"start": v(-7.93, 19.05) * mm, "mid": v(-10.15, 13.17) * mm, "end": v(-8.48, 7.1) * mm});
            skLineSegment(sketch, "E96.trimOffspring", {"start": v(7.93, 19.05) * mm, "end": v(25.4, 19.05) * mm});
            skLineSegment(sketch, "E97.trimOffspring", {"start": v(7.93, -19.05) * mm, "end": v(25.4, -19.05) * mm});
            skLineSegment(sketch, "E98.0.0", {"start": v(-38.1, 3.17) * mm, "end": v(-38.1, -3.18) * mm});
            skLineSegment(sketch, "E98.0.2", {"start": v(-38.1, -3.18) * mm, "end": v(-38.1, 3.17) * mm});
            skSolve(sketch);
        }
        {
            var Q0;
            Q0 = qSketchRegion(id + "F24", true);
            var Q1;
            Q1=makeQuery(id+"F21.opExtrude","CAP_FACE",FACE,{"disambiguationData":[OSD([sQuery(id+"F20.wireOp",EDGE,"E68")])],"isStart":false});
            extrude(context, id + "F25", {"entities" : qUnion([Q0]), "operationType" : NewBodyOperationType.ADD, "endBound" : BoundingType.UP_TO_SURFACE, "depth" : 25.4 * mm, "endBoundEntityFace" : qUnion([Q1]), "offsetDistance" : 25.4 * mm});
        }
        {
            var Q0;
            Q0=qCreatedBy(makeId("Front.planeOp"),FACE);
            var sketch = newSketch(context, id + "F26", { "sketchPlane" : qUnion([Q0])});
            skLineSegment(sketch, "E99", {"start": v(-12.7, 50.8) * mm, "end": v(-38.1, 44.45) * mm});
            skLineSegment(sketch, "E100", {"start": v(-38.1, 38.1) * mm, "end": v(-12.7, 38.1) * mm, "construction": true});
            skLineSegment(sketch, "E101", {"start": v(-12.7, 38.1) * mm, "end": v(-12.7, 50.8) * mm, "construction": true});
            skLineSegment(sketch, "E102", {"start": v(0, 27.16) * mm, "end": v(0, 60.15) * mm, "construction": true});
            skLineSegment(sketch, "E103", {"start": v(-38.1, 38.1) * mm, "end": v(-38.1, 44.45) * mm, "construction": true});
            skLineSegment(sketch, "E104", {"start": v(-38.1, 44.45) * mm, "end": v(-38.1, 50.8) * mm});
            skLineSegment(sketch, "E105", {"start": v(-38.1, 50.8) * mm, "end": v(-12.7, 50.8) * mm});
            skLineSegment(sketch, "E106.MirrorCS", {"start": v(12.7, 50.8) * mm, "end": v(38.1, 44.45) * mm});
            skLineSegment(sketch, "E107.MirrorCS", {"start": v(38.1, 50.8) * mm, "end": v(12.7, 50.8) * mm});
            skLineSegment(sketch, "E108.MirrorCS", {"start": v(38.1, 44.45) * mm, "end": v(38.1, 50.8) * mm});
            skSolve(sketch);
        }
        {
            var Q0;
            Q0 = qSketchRegion(id + "F26", true);
            extrude(context, id + "F27", {"entities" : qUnion([Q0]), "operationType" : NewBodyOperationType.REMOVE, "endBound" : BoundingType.SYMMETRIC, "oppositeDirection" : true, "depth" : 127 * mm, "offsetDistance" : 25.4 * mm});
        }
        {
            var Q0;
            Q0=qCreatedBy(makeId("Front.planeOp"),FACE);
            var sketch = newSketch(context, id + "F28", { "sketchPlane" : qUnion([Q0])});
            skLineSegment(sketch, "E109", {"start": v(-10.19, 50.8) * mm, "end": v(10.19, 50.8) * mm, "construction": true});
            skLineSegment(sketch, "E110", {"start": v(10.19, 50.8) * mm, "end": v(10.19, 38.1) * mm, "construction": true});
            skLineSegment(sketch, "E111", {"start": v(-10.19, 50.8) * mm, "end": v(-10.19, 38.1) * mm, "construction": true});
            skArc(sketch, "E112", {"start": v(10.19, 38.1) * mm, "mid": v(0, 47) * mm, "end": v(-10.19, 38.1) * mm});
            skLineSegment(sketch, "E113", {"start": v(-10.19, 50.8) * mm, "end": v(-12.7, 50.8) * mm, "construction": true});
            skLineSegment(sketch, "E114", {"start": v(-12.7, 50.8) * mm, "end": v(-12.7, 38.1) * mm});
            skLineSegment(sketch, "E115", {"start": v(-12.7, 38.1) * mm, "end": v(-10.19, 38.1) * mm});
            skLineSegment(sketch, "E116", {"start": v(10.19, 38.1) * mm, "end": v(12.7, 38.1) * mm});
            skLineSegment(sketch, "E117", {"start": v(12.7, 38.1) * mm, "end": v(12.7, 50.8) * mm});
            skLineSegment(sketch, "E118", {"start": v(12.7, 50.8) * mm, "end": v(10.19, 50.8) * mm, "construction": true});
            skLineSegment(sketch, "E119", {"start": v(-12.7, 50.8) * mm, "end": v(-12.7, 55.88) * mm});
            skLineSegment(sketch, "E120", {"start": v(-12.7, 55.88) * mm, "end": v(12.7, 55.88) * mm});
            skLineSegment(sketch, "E121", {"start": v(12.7, 55.88) * mm, "end": v(12.7, 50.8) * mm});
            skSolve(sketch);
        }
        {
            var Q0;
            Q0 = qSketchRegion(id + "F28", true);
            extrude(context, id + "F29", {"entities" : qUnion([Q0]), "operationType" : NewBodyOperationType.ADD, "endBound" : BoundingType.SYMMETRIC, "depth" : 38.1 * mm, "offsetDistance" : 25.4 * mm});
        }
        {
            var Q0;
            Q0=makeQuery(id+"F17.opExtrude","CAP_FACE",FACE,{"disambiguationData":[OSD([sQuery(id+"F16.wireOp",EDGE,"E59.0"),sQuery(id+"F16.wireOp",EDGE,"E60.0"),sQuery(id+"F16.wireOp",EDGE,"E61.0"),sQuery(id+"F16.wireOp",EDGE,"E62.0"),sQuery(id+"F16.wireOp",EDGE,"E63.0"),sQuery(id+"F16.wireOp",EDGE,"E64.0")])],"isStart":false});
            var sketch = newSketch(context, id + "F30", { "sketchPlane" : qUnion([Q0])});
            skCircle(sketch, "E122", {"center": v(0, 12.7) * mm, "radius": 5.71 * mm});
            skCircle(sketch, "E123", {"center": v(0, -12.7) * mm, "radius": 5.71 * mm});
            skCircle(sketch, "E124", {"center": v(0, -12.7) * mm, "radius": 7.62 * mm});
            skCircle(sketch, "E125", {"center": v(0, 12.7) * mm, "radius": 7.62 * mm});
            skSolve(sketch);
        }
        {
            var Q0;
            Q0 = qSketchRegion(id + "F30", true);
            extrude(context, id + "F31", {"entities" : qUnion([Q0]), "operationType" : NewBodyOperationType.ADD, "depth" : 1.9 * mm, "offsetDistance" : 25.4 * mm});
        }
        {
            var Q0;
            Q0=makeQuery(id+"F29.opExtrude","SWEPT_FACE",FACE,{"disambiguationData":[OSD([sQuery(id+"F28.wireOp",EDGE,"E120")])]});
            fillet(context, id + "F32", {"entities" : qUnion([Q0]), "radius" : 5.08 * mm, "tangentPropagation" : true, "allowEdgeOverflow" : false});
        }
        {
            var Q0;
            Q0=makeQuery(id+"F19.opExtrude","CAP_FACE",FACE,{"disambiguationData":[OSD([sQuery(id+"F18.wireOp",EDGE,"E65")])],"isStart":true});
            var sketch = newSketch(context, id + "F33", { "sketchPlane" : qUnion([Q0])});
            skCircle(sketch, "E126.0.0", {"center": v(0, 12.7) * mm, "radius": 3.18 * mm});
            skCircle(sketch, "E127.0.0", {"center": v(0, -12.7) * mm, "radius": 3.18 * mm});
            skSolve(sketch);
        }
        {
            var Q0;
            Q0 = qSketchRegion(id + "F33", true);
            extrude(context, id + "F34", {"entities" : qUnion([Q0]), "operationType" : NewBodyOperationType.REMOVE, "oppositeDirection" : true, "depth" : 21.59 * mm, "offsetDistance" : 25.4 * mm});
        }
        {
            var Q0;
            Q0=makeQuery(id+"F6.opExtrude","CAP_FACE",FACE,{"disambiguationData":[OSD([sQuery(id+"F5.wireOp",EDGE,"E31.0.0"),sQuery(id+"F5.wireOp",EDGE,"E31.0.1"),sQuery(id+"F5.wireOp",EDGE,"E31.0.2"),sQuery(id+"F5.wireOp",EDGE,"E31.0.3"),sQuery(id+"F5.wireOp",EDGE,"E31.0.4"),sQuery(id+"F5.wireOp",EDGE,"E31.0.5"),sQuery(id+"F5.wireOp",EDGE,"E31.0.6"),sQuery(id+"F5.wireOp",EDGE,"E31.0.7"),sQuery(id+"F5.wireOp",EDGE,"E31.0.8"),sQuery(id+"F5.wireOp",EDGE,"E31.0.9"),sQuery(id+"F5.wireOp",EDGE,"E31.0.10"),sQuery(id+"F5.wireOp",EDGE,"E31.0.11"),sQuery(id+"F5.wireOp",EDGE,"E31.0.12"),sQuery(id+"F5.wireOp",EDGE,"E31.0.13"),sQuery(id+"F5.wireOp",EDGE,"E31.0.14"),sQuery(id+"F5.wireOp",EDGE,"E31.0.15"),sQuery(id+"F5.wireOp",EDGE,"E31.0.16"),sQuery(id+"F5.wireOp",EDGE,"E31.0.17"),sQuery(id+"F5.wireOp",EDGE,"E31.0.18"),sQuery(id+"F5.wireOp",EDGE,"E31.0.19"),sQuery(id+"F5.wireOp",EDGE,"E34.0"),sQuery(id+"F5.wireOp",EDGE,"E35.0"),sQuery(id+"F5.wireOp",EDGE,"E36.0"),sQuery(id+"F5.wireOp",EDGE,"E37.0"),sQuery(id+"F5.wireOp",EDGE,"E38"),sQuery(id+"F5.wireOp",EDGE,"E39")])],"isStart":true});
            chamfer(context, id + "F35", {"entities" : qUnion([Q0]), "width" : 0.89 * mm, "tangentPropagation" : true});
        }
    });
